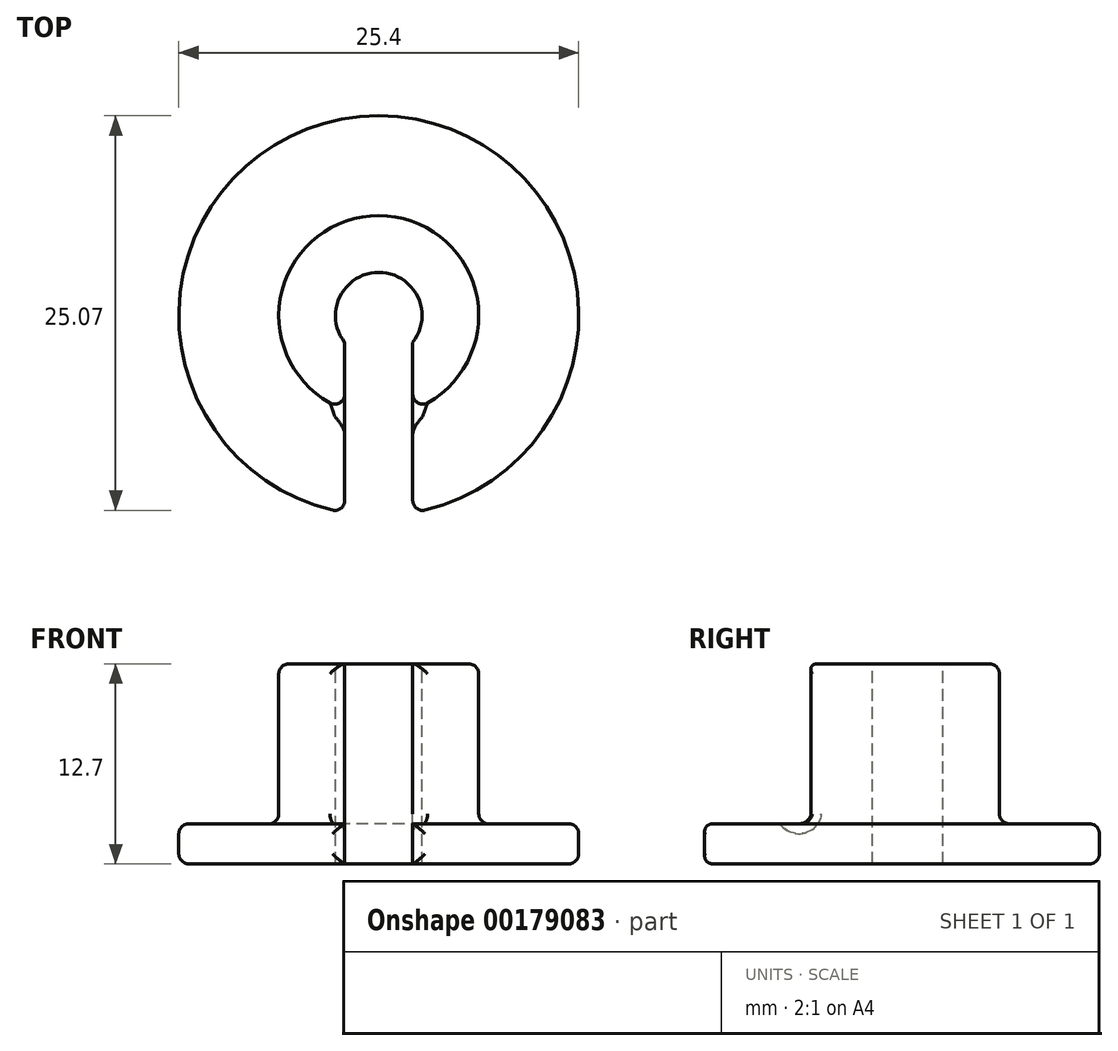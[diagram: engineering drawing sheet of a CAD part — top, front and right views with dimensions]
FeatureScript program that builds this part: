
annotation { "Feature Type Name" : "Feature", "Feature Type Description" : "" }
export const myFeature = defineFeature(function(context is Context, id is Id, definition is map)
    precondition{}
    {
        {
            var Q0;
            Q0=qCreatedBy(makeId("Top.planeOp"),FACE);
            var sketch = newSketch(context, id + "F0", { "sketchPlane" : qUnion([Q0])});
            skCircle(sketch, "E0", {"center": v(0, 0) * mm, "radius": 12.7 * mm});
            skCircle(sketch, "E1", {"center": v(0, 0) * mm, "radius": 2.29 * mm});
            skSolve(sketch);
        }
        {
            var Q0;
            Q0 = qSketchRegion(id + "F0", true);
            extrude(context, id + "F1", {"entities" : qUnion([Q0]), "depth" : 2.54 * mm});
        }
        {
            var Q0;
            Q0=makeQuery(id+"F1.opExtrude","CAP_FACE",FACE,{"disambiguationData":[OSD([sQuery(id+"F0.wireOp",EDGE,"E0"),sQuery(id+"F0.wireOp",EDGE,"E1")])],"isStart":false});
            var sketch = newSketch(context, id + "F2", { "sketchPlane" : qUnion([Q0])});
            skCircle(sketch, "E2.0", {"center": v(0, 0) * mm, "radius": 2.29 * mm});
            skCircle(sketch, "E3", {"center": v(0, 0) * mm, "radius": 6.35 * mm});
            skSolve(sketch);
        }
        {
            var Q0;
            Q0 = qSketchRegion(id + "F2", true);
            extrude(context, id + "F3", {"entities" : qUnion([Q0]), "operationType" : NewBodyOperationType.ADD, "depth" : 10.16 * mm});
        }
        {
            var Q0;
            Q0=makeQuery(id+"F3.opExtrude","CAP_FACE",FACE,{"disambiguationData":[OSD([sQuery(id+"F2.wireOp",EDGE,"E2.0"),sQuery(id+"F2.wireOp",EDGE,"E3")])],"isStart":false});
            var sketch = newSketch(context, id + "F4", { "sketchPlane" : qUnion([Q0])});
            skLineSegment(sketch, "E4", {"start": v(0, 0) * mm, "end": v(0, -16.14) * mm, "construction": true});
            skLineSegment(sketch, "E5", {"start": v(-2.16, -0.75) * mm, "end": v(-2.16, -14.49) * mm});
            skLineSegment(sketch, "E6", {"start": v(2.16, -0.75) * mm, "end": v(2.16, -14.14) * mm});
            skLineSegment(sketch, "E7", {"start": v(2.16, -14.14) * mm, "end": v(-2.16, -14.49) * mm});
            skArc(sketch, "E8.0", {"start": v(-2.16, -0.75) * mm, "mid": v(0, -2.29) * mm, "end": v(2.16, -0.75) * mm});
            skSolve(sketch);
        }
        {
            var Q0;
            Q0 = qSketchRegion(id + "F4", true);
            extrude(context, id + "F5", {"entities" : qUnion([Q0]), "operationType" : NewBodyOperationType.REMOVE, "endBound" : BoundingType.THROUGH_ALL, "oppositeDirection" : true, "depth" : 25.4 * mm});
        }
        {
            var Q0;
            Q0=makeQuery(id+"F3.opExtrude","SWEPT_FACE",FACE,{"disambiguationData":[OSD([sQuery(id+"F2.wireOp",EDGE,"E3")])]});
            fillet(context, id + "F6", {"entities" : qUnion([Q0]), "radius" : 0.64 * mm, "tangentPropagation" : true, "allowEdgeOverflow" : false});
        }
        {
            var Q0;
            Q0=makeQuery(id+"F1.opExtrude","SWEPT_FACE",FACE,{"disambiguationData":[OSD([sQuery(id+"F0.wireOp",EDGE,"E0")])]});
            fillet(context, id + "F7", {"entities" : qUnion([Q0]), "radius" : 0.64 * mm, "tangentPropagation" : true, "allowEdgeOverflow" : false});
        }
        {
            var Q0;
            Q0=makeQuery(id+"F3.opExtrude","CAP_FACE",FACE,{"disambiguationData":[OSD([sQuery(id+"F2.wireOp",EDGE,"E2.0"),sQuery(id+"F2.wireOp",EDGE,"E3")])],"isStart":false});
            var sketch = newSketch(context, id + "F8", { "sketchPlane" : qUnion([Q0])});
            skCircle(sketch, "E9", {"center": v(0, 0) * mm, "radius": 2.75 * mm});
            skSolve(sketch);
        }
        {
            var Q0;
            Q0 = qSketchRegion(id + "F8", true);
            extrude(context, id + "F9", {"entities" : qUnion([Q0]), "operationType" : NewBodyOperationType.REMOVE, "oppositeDirection" : true, "depth" : 25.4 * mm});
        }
    });
